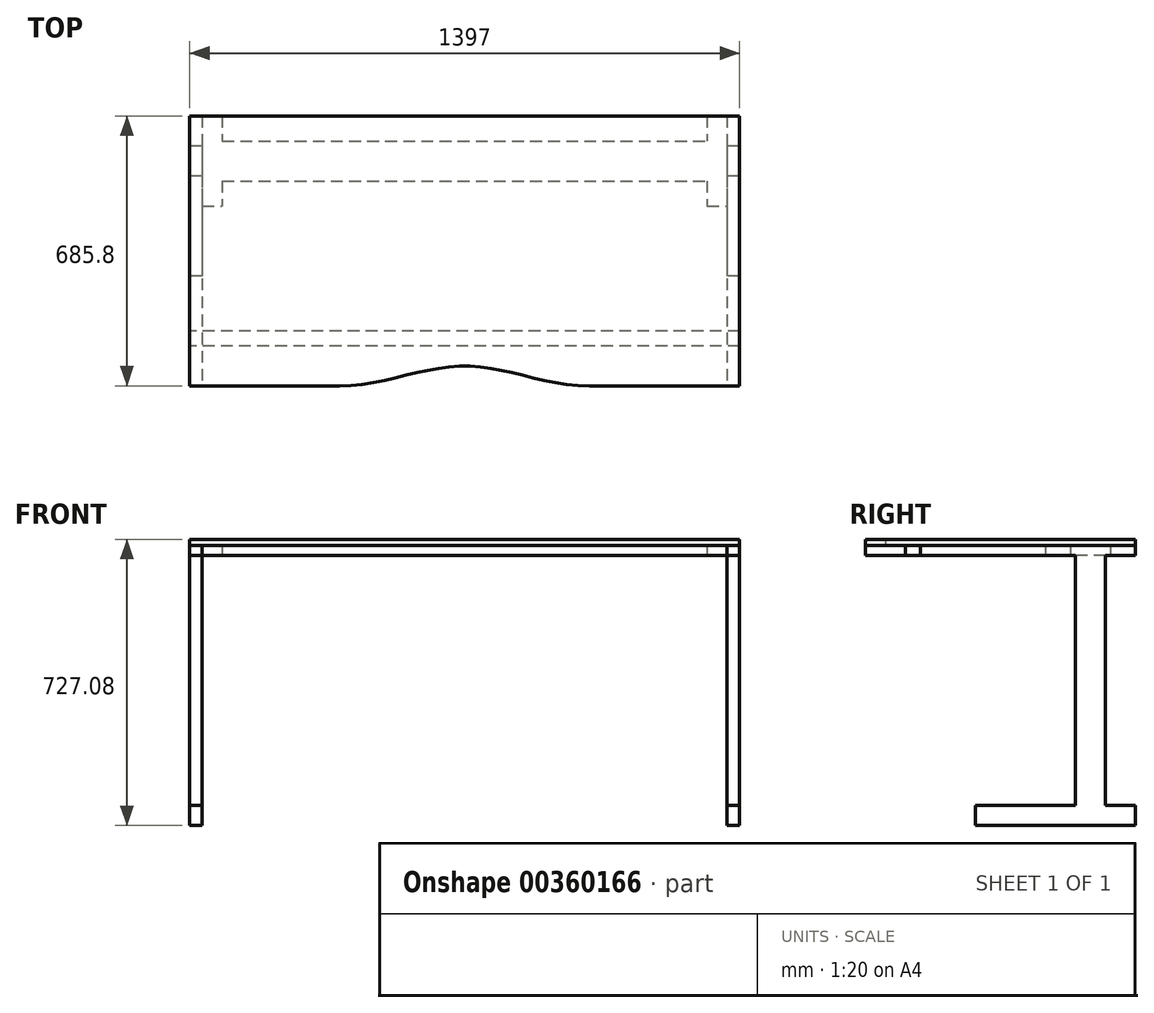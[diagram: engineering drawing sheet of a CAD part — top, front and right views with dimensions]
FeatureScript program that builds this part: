
annotation { "Feature Type Name" : "Feature", "Feature Type Description" : "" }
export const myFeature = defineFeature(function(context is Context, id is Id, definition is map)
    precondition{}
    {
        {
            var Q0;
            Q0=qCreatedBy(makeId("Top.planeOp"),FACE);
            var sketch = newSketch(context, id + "F0", { "sketchPlane" : qUnion([Q0])});
            skLineSegment(sketch, "E0.bottom", {"start": v(0, 0) * mm, "end": v(381, 0) * mm});
            skLineSegment(sketch, "E0.top", {"start": v(0, 685.8) * mm, "end": v(1397, 685.8) * mm});
            skLineSegment(sketch, "E0.left", {"start": v(0, 0) * mm, "end": v(0, 685.8) * mm});
            skLineSegment(sketch, "E0.right", {"start": v(1397, 0) * mm, "end": v(1397, 685.8) * mm});
            skPoint(sketch, "E1", {"position": v(1016, 0) * mm});
            skPoint(sketch, "E2", {"position": v(381, 0) * mm});
            skPoint(sketch, "E3", {"position": v(698.5, 50.8) * mm});
            skLineSegment(sketch, "E4.trimOffspring", {"start": v(1016, 0) * mm, "end": v(1397, 0) * mm});
            skFitSpline(sketch, "E5", {"points": [v(381, 0) * mm, v(698.5, 50.8) * mm, v(1016, 0) * mm], "startDerivative": vector(659.31, 0) * mm, "endDerivative": vector(699.63, 0) * mm});
            skSolve(sketch);
        }
        {
            var Q0;
            Q0=qSketchRegion(id+"F0",true);
            extrude(context, id + "F1", {"entities" : qUnion([Q0]), "depth" : 15.88 * mm});
        }
        {
            var Q0;
            Q0=makeQuery(id+"F1.opExtrude","SWEPT_FACE",FACE,{"disambiguationData":[OSD([sQuery(id+"F0.wireOp",EDGE,"E0.left")])]});
            var sketch = newSketch(context, id + "F2", { "sketchPlane" : qUnion([Q0])});
            skPoint(sketch, "E6", {"position": v(-609.6, 0) * mm});
            skPoint(sketch, "E7", {"position": v(-533.4, 0) * mm});
            skLineSegment(sketch, "E8.bottom", {"start": v(-609.6, 0) * mm, "end": v(-533.4, 0) * mm});
            skLineSegment(sketch, "E8.top", {"start": v(-609.6, -711.2) * mm, "end": v(-533.4, -711.2) * mm});
            skLineSegment(sketch, "E8.left", {"start": v(-609.6, 0) * mm, "end": v(-609.6, -711.2) * mm});
            skLineSegment(sketch, "E8.right", {"start": v(-533.4, 0) * mm, "end": v(-533.4, -711.2) * mm});
            skLineSegment(sketch, "E9.bottom", {"start": v(-685.8, 0) * mm, "end": v(0, 0) * mm});
            skLineSegment(sketch, "E9.top", {"start": v(-685.8, -25.4) * mm, "end": v(0, -25.4) * mm});
            skLineSegment(sketch, "E9.left", {"start": v(-685.8, 0) * mm, "end": v(-685.8, -25.4) * mm});
            skLineSegment(sketch, "E9.right", {"start": v(0, 0) * mm, "end": v(0, -25.4) * mm});
            skSolve(sketch);
        }
        {
            var Q0;
            Q0=qSketchRegion(id+"F2",true);
            extrude(context, id + "F3", {"entities" : qUnion([Q0]), "oppositeDirection" : true, "depth" : 1397 * mm});
        }
        {
            var Q0;
            Q0=makeQuery(id+"F3.opExtrude","SWEPT_FACE",FACE,{"disambiguationData":[OSD([sQuery(id+"F2.wireOp",EDGE,"E8.right")])]});
            var sketch = newSketch(context, id + "F4", { "sketchPlane" : qUnion([Q0])});
            skPoint(sketch, "E10", {"position": v(31.75, -711.2) * mm});
            skLineSegment(sketch, "E11.left", {"start": v(31.75, -711.2) * mm, "end": v(31.75, -711.2) * mm});
            skLineSegment(sketch, "E11.right", {"start": v(1365.25, -711.2) * mm, "end": v(1365.25, -711.2) * mm});
            skLineSegment(sketch, "E12.bottom", {"start": v(31.75, -711.2) * mm, "end": v(1365.25, -711.2) * mm});
            skLineSegment(sketch, "E12.top", {"start": v(31.75, -25.4) * mm, "end": v(1365.25, -25.4) * mm});
            skLineSegment(sketch, "E12.left", {"start": v(31.75, -711.2) * mm, "end": v(31.75, -25.4) * mm});
            skLineSegment(sketch, "E12.right", {"start": v(1365.25, -711.2) * mm, "end": v(1365.25, -25.4) * mm});
            skSolve(sketch);
        }
        {
            var Q0;
            Q0=qSketchRegion(id+"F4",true);
            extrude(context, id + "F5", {"entities" : qUnion([Q0]), "operationType" : NewBodyOperationType.REMOVE, "oppositeDirection" : true, "depth" : 76.2 * mm});
        }
        {
            var Q0;
            Q0=makeQuery(id+"F3.boolean.opBoolean","MERGE",FACE,{"derivedFrom":[makeQuery(id+"F1.opExtrude","SWEPT_FACE",FACE,{"disambiguationData":[OSD([sQuery(id+"F0.wireOp",EDGE,"E0.bottom")])]}),makeQuery(id+"F1.opExtrude","SWEPT_FACE",FACE,{"disambiguationData":[OSD([sQuery(id+"F0.wireOp",EDGE,"E4.trimOffspring")])]}),makeQuery(id+"F3.opExtrude","SWEPT_FACE",FACE,{"disambiguationData":[OSD([sQuery(id+"F2.wireOp",EDGE,"E9.right")])]})]});
            var sketch = newSketch(context, id + "F6", { "sketchPlane" : qUnion([Q0])});
            skPoint(sketch, "E13", {"position": v(31.75, -25.4) * mm});
            skLineSegment(sketch, "E14.bottom", {"start": v(31.75, -25.4) * mm, "end": v(1365.25, -25.4) * mm});
            skLineSegment(sketch, "E14.top", {"start": v(31.75, 0) * mm, "end": v(1365.25, 0) * mm});
            skLineSegment(sketch, "E14.left", {"start": v(31.75, -25.4) * mm, "end": v(31.75, 0) * mm});
            skLineSegment(sketch, "E14.right", {"start": v(1365.25, -25.4) * mm, "end": v(1365.25, 0) * mm});
            skSolve(sketch);
        }
        {
            var Q0;
            Q0=qSketchRegion(id+"F6",true);
            extrude(context, id + "F7", {"entities" : qUnion([Q0]), "operationType" : NewBodyOperationType.REMOVE, "oppositeDirection" : true, "depth" : 457.2 * mm});
        }
        {
            var Q0;
            Q0=makeQuery(id+"F3.opExtrude","CAP_FACE",FACE,{"disambiguationData":[OSD([sQuery(id+"F2.wireOp",EDGE,"E8.top"),sQuery(id+"F2.wireOp",EDGE,"E8.left"),sQuery(id+"F2.wireOp",EDGE,"E8.right"),sQuery(id+"F2.wireOp",EDGE,"E9.bottom"),sQuery(id+"F2.wireOp",EDGE,"E9.top"),sQuery(id+"F2.wireOp",EDGE,"E9.left"),sQuery(id+"F2.wireOp",EDGE,"E9.right")])],"isStart":true});
            var sketch = newSketch(context, id + "F8", { "sketchPlane" : qUnion([Q0])});
            skPoint(sketch, "E15", {"position": v(-685.8, -711.2) * mm});
            skPoint(sketch, "E16", {"position": v(-685.8, -660.4) * mm});
            skPoint(sketch, "E17", {"position": v(-279.4, -711.2) * mm});
            skPoint(sketch, "E18", {"position": v(-279.4, -660.4) * mm});
            skLineSegment(sketch, "E19.bottom", {"start": v(-685.8, -711.2) * mm, "end": v(-279.4, -711.2) * mm});
            skLineSegment(sketch, "E19.top", {"start": v(-685.8, -660.4) * mm, "end": v(-279.4, -660.4) * mm});
            skLineSegment(sketch, "E19.left", {"start": v(-685.8, -711.2) * mm, "end": v(-685.8, -660.4) * mm});
            skLineSegment(sketch, "E19.right", {"start": v(-279.4, -711.2) * mm, "end": v(-279.4, -660.4) * mm});
            skSolve(sketch);
        }
        {
            var Q0;
            Q0=qSketchRegion(id+"F8",true);
            extrude(context, id + "F9", {"entities" : qUnion([Q0]), "operationType" : NewBodyOperationType.ADD, "oppositeDirection" : true, "depth" : 1397 * mm});
        }
        {
            var Q0;
            Q0=makeQuery(id+"F9.opExtrude","SWEPT_FACE",FACE,{"disambiguationData":[OSD([sQuery(id+"F8.wireOp",EDGE,"E19.right")])]});
            var sketch = newSketch(context, id + "F10", { "sketchPlane" : qUnion([Q0])});
            skPoint(sketch, "E20", {"position": v(31.75, -711.2) * mm});
            skPoint(sketch, "E21", {"position": v(31.75, -660.4) * mm});
            skLineSegment(sketch, "E22.bottom", {"start": v(31.75, -711.2) * mm, "end": v(1365.25, -711.2) * mm});
            skLineSegment(sketch, "E22.top", {"start": v(31.75, -660.4) * mm, "end": v(1365.25, -660.4) * mm});
            skLineSegment(sketch, "E22.left", {"start": v(31.75, -711.2) * mm, "end": v(31.75, -660.4) * mm});
            skLineSegment(sketch, "E22.right", {"start": v(1365.25, -711.2) * mm, "end": v(1365.25, -660.4) * mm});
            skSolve(sketch);
        }
        {
            var Q0;
            Q0=qSketchRegion(id+"F10",true);
            extrude(context, id + "F11", {"entities" : qUnion([Q0]), "operationType" : NewBodyOperationType.REMOVE, "oppositeDirection" : true, "depth" : 457.2 * mm});
        }
        {
            var Q0;
            Q0=makeQuery(id+"F9.boolean.opBoolean","MERGE",FACE,{"derivedFrom":[makeQuery(id+"F3.opExtrude","CAP_FACE",FACE,{"disambiguationData":[OSD([sQuery(id+"F2.wireOp",EDGE,"E8.top"),sQuery(id+"F2.wireOp",EDGE,"E8.left"),sQuery(id+"F2.wireOp",EDGE,"E8.right"),sQuery(id+"F2.wireOp",EDGE,"E9.bottom"),sQuery(id+"F2.wireOp",EDGE,"E9.top"),sQuery(id+"F2.wireOp",EDGE,"E9.left"),sQuery(id+"F2.wireOp",EDGE,"E9.right")])],"isStart":true}),makeQuery(id+"F9.opExtrude","CAP_FACE",FACE,{"disambiguationData":[OSD([sQuery(id+"F8.wireOp",EDGE,"E19.bottom"),sQuery(id+"F8.wireOp",EDGE,"E19.top"),sQuery(id+"F8.wireOp",EDGE,"E19.left"),sQuery(id+"F8.wireOp",EDGE,"E19.right")])],"isStart":true})]});
            var sketch = newSketch(context, id + "F12", { "sketchPlane" : qUnion([Q0])});
            skPoint(sketch, "E23", {"position": v(-101.6, -25.4) * mm});
            skPoint(sketch, "E24", {"position": v(-139.7, -25.4) * mm});
            skLineSegment(sketch, "E25.bottom", {"start": v(-139.7, -25.4) * mm, "end": v(-101.6, -25.4) * mm});
            skLineSegment(sketch, "E25.top", {"start": v(-139.7, 0) * mm, "end": v(-101.6, 0) * mm});
            skLineSegment(sketch, "E25.left", {"start": v(-139.7, -25.4) * mm, "end": v(-139.7, 0) * mm});
            skLineSegment(sketch, "E25.right", {"start": v(-101.6, -25.4) * mm, "end": v(-101.6, 0) * mm});
            skSolve(sketch);
        }
        {
            var Q0;
            Q0=qSketchRegion(id+"F12",true);
            extrude(context, id + "F13", {"entities" : qUnion([Q0]), "oppositeDirection" : true, "depth" : 1397 * mm});
        }
        {
            var Q0;
            {var subQ0=sQuery(id+"F2.wireOp",EDGE,"E9.top");Q0=makeQuery(id+"F5.boolean.opBoolean","MERGE",FACE,{"derivedFrom":[makeQuery(id+"F3.opExtrude","SWEPT_FACE",FACE,{"disambiguationData":[OSD([subQ0]),TDD([makeQuery(id+"F2.imprint","IMPRINT",EDGE,{"disambiguationData":[TD([[makeQuery(id+"F2.imprint","INTERSECT",VERTEX,{"derivedFrom":[subQ0,sQuery(id+"F2.wireOp",EDGE,"E9.left")]}),-1.0]])],"derivedFrom":subQ0})])]}),makeQuery(id+"F3.opExtrude","SWEPT_FACE",FACE,{"disambiguationData":[OSD([subQ0]),TDD([makeQuery(id+"F2.imprint","IMPRINT",EDGE,{"disambiguationData":[TD([[makeQuery(id+"F2.imprint","INTERSECT",VERTEX,{"derivedFrom":[subQ0,sQuery(id+"F2.wireOp",EDGE,"E9.right")]}),1.0]])],"derivedFrom":subQ0})])]}),makeQuery(id+"F5.opExtrude","SWEPT_FACE",FACE,{"disambiguationData":[OSD([sQuery(id+"F4.wireOp",EDGE,"E12.top")])]})]});}
            var sketch = newSketch(context, id + "F14", { "sketchPlane" : qUnion([Q0])});
            skPoint(sketch, "E26", {"position": v(82.55, -685.8) * mm});
            skPoint(sketch, "E27", {"position": v(1314.45, -685.8) * mm});
            skLineSegment(sketch, "E28.bottom", {"start": v(82.55, -685.8) * mm, "end": v(1314.45, -685.8) * mm});
            skLineSegment(sketch, "E28.top", {"start": v(82.55, -622.3) * mm, "end": v(1314.45, -622.3) * mm});
            skLineSegment(sketch, "E28.left", {"start": v(82.55, -685.8) * mm, "end": v(82.55, -622.3) * mm});
            skLineSegment(sketch, "E28.right", {"start": v(1314.45, -685.8) * mm, "end": v(1314.45, -622.3) * mm});
            skPoint(sketch, "E29", {"position": v(82.55, -520.7) * mm});
            skPoint(sketch, "E30", {"position": v(1314.45, -520.7) * mm});
            skPoint(sketch, "E31", {"position": v(1314.45, -457.2) * mm});
            skLineSegment(sketch, "E32.bottom", {"start": v(82.55, -520.7) * mm, "end": v(1314.45, -520.7) * mm});
            skLineSegment(sketch, "E32.top", {"start": v(82.55, -457.2) * mm, "end": v(1314.45, -457.2) * mm});
            skLineSegment(sketch, "E32.left", {"start": v(82.55, -520.7) * mm, "end": v(82.55, -457.2) * mm});
            skLineSegment(sketch, "E32.right", {"start": v(1314.45, -520.7) * mm, "end": v(1314.45, -457.2) * mm});
            skSolve(sketch);
        }
        {
            var Q0;
            Q0=qSketchRegion(id+"F14",true);
            extrude(context, id + "F15", {"entities" : qUnion([Q0]), "operationType" : NewBodyOperationType.REMOVE, "oppositeDirection" : true, "depth" : 25.4 * mm});
        }
    });
